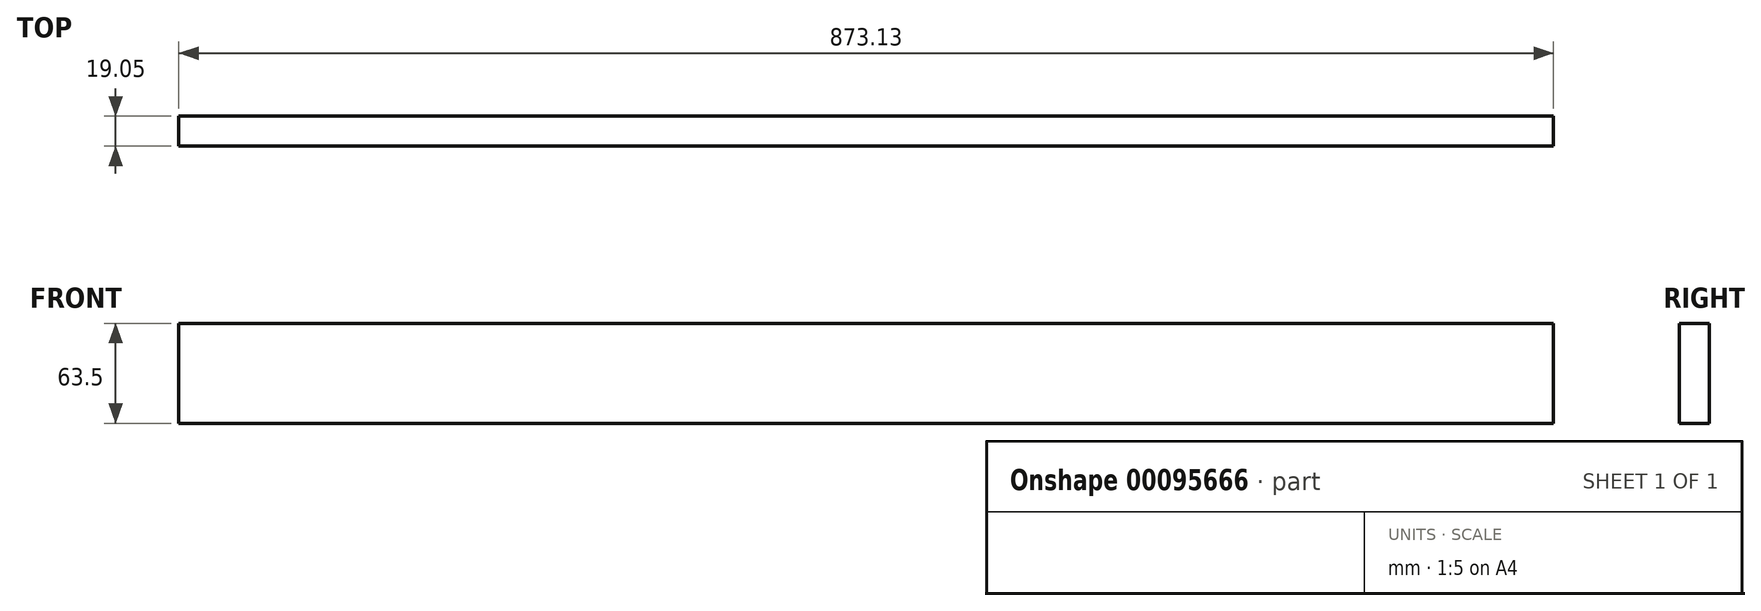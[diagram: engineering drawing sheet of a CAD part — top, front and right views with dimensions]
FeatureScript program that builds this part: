
annotation { "Feature Type Name" : "Feature", "Feature Type Description" : "" }
export const myFeature = defineFeature(function(context is Context, id is Id, definition is map)
    precondition{}
    {
        {
            var Q0;
            Q0=qCreatedBy(makeId("Front.planeOp"),FACE);
            var sketch = newSketch(context, id + "F0", { "sketchPlane" : qUnion([Q0])});
            skLineSegment(sketch, "E0.bottom", {"start": v(-468.5, -80.39) * mm, "end": v(404.63, -80.39) * mm});
            skLineSegment(sketch, "E0.top", {"start": v(-468.5, -143.89) * mm, "end": v(404.63, -143.89) * mm});
            skLineSegment(sketch, "E0.left", {"start": v(-468.5, -80.39) * mm, "end": v(-468.5, -143.89) * mm});
            skLineSegment(sketch, "E0.right", {"start": v(404.63, -80.39) * mm, "end": v(404.63, -143.89) * mm});
            skSolve(sketch);
        }
        {
            var Q0;
            Q0=makeQuery(id+"F0.imprint","IMPRINT",FACE,{"disambiguationData":[TD([[makeQuery(id+"F0.imprint","IMPRINT",EDGE,{"derivedFrom":sQuery(id+"F0.wireOp",EDGE,"E0.bottom")}),-1.0]])]});
            extrude(context, id + "F1", {"entities" : qUnion([Q0]), "depth" : 19.05 * mm});
        }
    });
